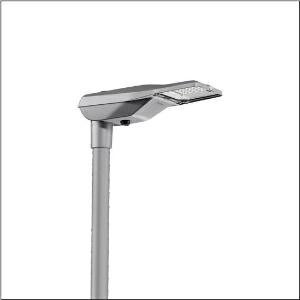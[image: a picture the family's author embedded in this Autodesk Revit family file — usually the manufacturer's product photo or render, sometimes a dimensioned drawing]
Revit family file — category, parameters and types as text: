
# Revit family: streetlight_sl_21_iq_micro___st1_0a_5xe1d31u08db_5c5a
name_source: partatom
category: Lighting Fixtures
units: mm (PartAtom-declared; Revit-internal decimal feet)

## family parameters
Cut with Voids When Loaded = No
Host = Face
Light Source = No
Part Type = Normal
Room Calculation Point = No
Round Connector Dimension = Use Diameter
Shared = No

## types (1)
- --- (1 x LED, 5110 lm, 39.1 W, 3000K)
    Apparent Load = 39 VA
    CIE Flux Codes = 37 72 97 100 100
    Color Rendering = 70
    Color Temperature = 3000K
    Default Elevation = 1800 mm
    Description = Streetlight SL 21 iQ micro, mast luminaire, primary light control with lens, of PMMA, primary optical cover: cover, of toughened safety glass, transparent, light distribution: ST1.0a, light emission: direct distribution, primary light characteristic: asymmetric, installation type: post-top, side-entry, LED, High Power LED, rated luminous flux: 5.110lm, luminous efficacy: 131lm/W, light colour: 730, colour temperature: 3000K, control: presetting dimming logarithmic, Street-Remote, Auto-Match, Temp-Guard, Lumen-Switch, Night-Set, Smart-Wire, Light-Fading, Desk-Remote (wireless, voltage-free reading and setting of iQ features in the workshop via application-optimized NFC function/RFID function), optimised constant luminous flux control (CLO 2.0), mains connection: 220..240V, AC, 50/60Hz, start of lifetime: 39W, end of service life: 41W, reduction: 17W, luminaire housing, of diecast aluminium, powder-coated, Siteco® metallic grey (DB 702S), corrosivity category C5 mid according to DIN EN ISO 12944, please order mast flange separately, inclination adjustable: 0°, 5°, 10°, 15°, sealing non-destructively replaceable, multi-level sealing system, length: 528mm, width: 235mm, height: 110mm, mast flange for spigot size: 42mm (side-entry): 5XC10008XM4, 60/48mm (side-entry/post-top): 5XC10108XM2, 76/60mm (side-entry/post-top): 5XC10108XM1, Smart Interface below, protection rating (complete): IP66, insulation class (complete): insulation class II (safety insulation), certification: CE, ENEC, ENEC+, VDE, impact resistance: IK09, permissible operating ambient temperature for outdoor applications: -40..+50°C, standard-compliant lighting for roads and squares, packaging unit: 1 piece

Light Distribution: ST1.0a
    Height = 110 mm
    Lamp = 1 x LED
    Lamp Light Flux = 5110 lm
    Lamp Power = 39.1 W
    Lamp count = 1
    Length = 528 mm
    Luminous efficacy = 131 lm/W
    Manufacturer = Siteco
    ModVariant = No
    Model = 5XE1D31U08DB
    Number of Poles = 1
    OnlyDefault = Yes
    Power Factor = 1
    Product Name = Streetlight SL 21 iQ micro | ST1.0a
    Product group = mast luminaire | pylon top
    ProductGroupID = 6100
    Protection Class = Protection class II
    Protection Degree = IP 66
    RLX_Detail_Level = 1
    RLX_Emergency_Light_Flux = 0 lm
    RLX_Emergency_Type = 0
    RLX_Emergency_Type_DB = No
    RlxData = <blob elided: 99389 chars, md5=9be899fb>
    Socket = socket
    Standby Power = 0 W
    System Light Flux = 5110 lm
    System Power = 39 W
    Type Comments = factory setting: luminous flux: 100 % | dim-lin: 254 | 765 mA
    Type Image = l_1277290.jpg
    URL = http://relux.com
    VarID = @adj_063919
    Voltage = 0 V
    Weight = 0.00 kg
    Width = 235 mm

## geometry (parser evidence)
native form markers: Blend x4, Sweep x9
no freeform markers — native parametric forms only
